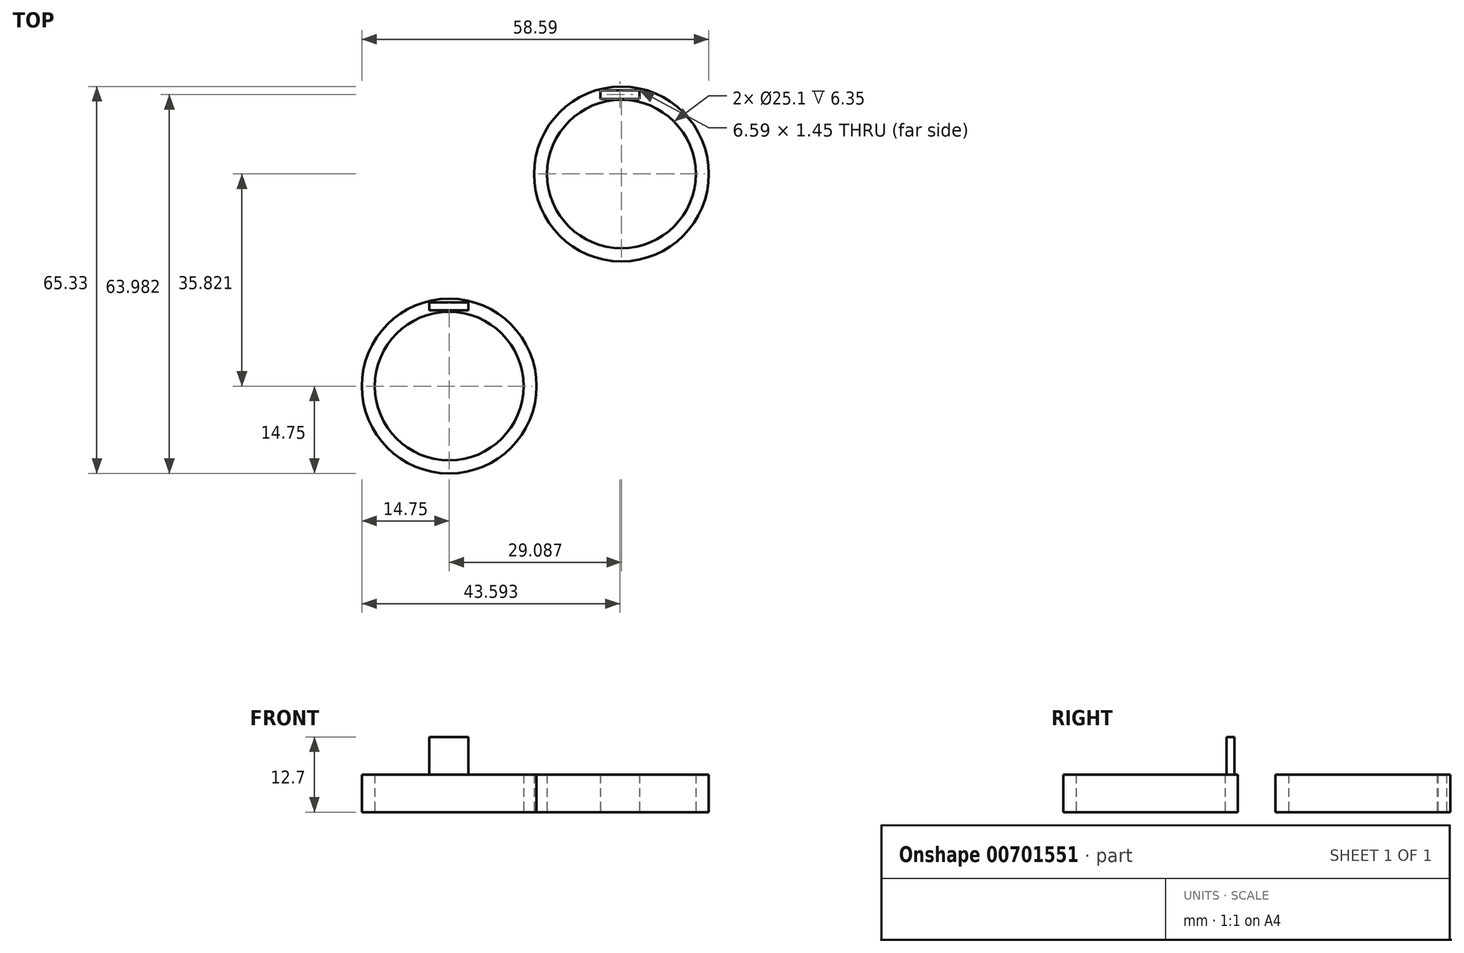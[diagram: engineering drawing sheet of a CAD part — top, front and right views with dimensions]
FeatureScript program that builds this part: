
annotation { "Feature Type Name" : "Feature", "Feature Type Description" : "" }
export const myFeature = defineFeature(function(context is Context, id is Id, definition is map)
    precondition{}
    {
        {
            var Q0;
            Q0=qCreatedBy(makeId("Top.planeOp"),FACE);
            var sketch = newSketch(context, id + "F0", { "sketchPlane" : qUnion([Q0])});
            skCircle(sketch, "E0", {"center": v(0, 0) * mm, "radius": 12.55 * mm});
            skCircle(sketch, "E1", {"center": v(0, 0) * mm, "radius": 14.75 * mm});
            skCircle(sketch, "E2", {"center": v(29.09, 35.82) * mm, "radius": 12.55 * mm});
            skCircle(sketch, "E3", {"center": v(29.09, 35.82) * mm, "radius": 14.76 * mm});
            skLineSegment(sketch, "E4.bottom", {"start": v(25.55, 49.96) * mm, "end": v(32.14, 49.96) * mm});
            skLineSegment(sketch, "E4.top", {"start": v(25.55, 48.5) * mm, "end": v(32.14, 48.5) * mm});
            skLineSegment(sketch, "E4.left", {"start": v(25.55, 49.96) * mm, "end": v(25.55, 48.5) * mm});
            skLineSegment(sketch, "E4.right", {"start": v(32.14, 49.96) * mm, "end": v(32.14, 48.5) * mm});
            skSolve(sketch);
        }
        {
            var Q0;
            Q0 = qSketchRegion(id + "F0", true);
            extrude(context, id + "F1", {"entities" : qUnion([Q0]), "depth" : 6.35 * mm, "offsetDistance" : 25.4 * mm});
        }
        {
            var Q0;
            Q0=qCreatedBy(makeId("Top.planeOp"),FACE);
            var sketch = newSketch(context, id + "F2", { "sketchPlane" : qUnion([Q0])});
            skLineSegment(sketch, "E5.bottom", {"start": v(-3.36, 14.13) * mm, "end": v(3.24, 14.13) * mm});
            skLineSegment(sketch, "E5.top", {"start": v(-3.36, 12.8) * mm, "end": v(3.24, 12.8) * mm});
            skLineSegment(sketch, "E5.left", {"start": v(-3.36, 14.13) * mm, "end": v(-3.36, 12.8) * mm});
            skLineSegment(sketch, "E5.right", {"start": v(3.24, 14.13) * mm, "end": v(3.24, 12.8) * mm});
            skSolve(sketch);
        }
        {
            var Q0;
            Q0 = qSketchRegion(id + "F2", true);
            extrude(context, id + "F3", {"entities" : qUnion([Q0]), "operationType" : NewBodyOperationType.ADD, "depth" : 12.7 * mm, "offsetDistance" : 25.4 * mm});
        }
    });
